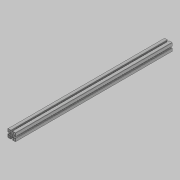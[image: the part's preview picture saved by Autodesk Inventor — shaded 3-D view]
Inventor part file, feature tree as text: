
AUTODESK INVENTOR PART (.ipt)
format: ipt  version: 2021.2 (Build 252289000, 289)  size: 202,240 bytes
history: native  units: in
note: dims shown in document units (in); Inventor stores cm internally (conversion verified against a paired STEP export)
features: other x2, extrude x1, sketch x1, projected_geometry x1
ambient origin geometry x8: Origin, YZ Plane, XZ Plane, XY Plane, X Axis, Y Axis, Z Axis, Center Point
bodies: Body1 (feature_tree)
feature tree (5):
  other  "ソリッド2"
  extrude  "押し出し1"  Depth=23.622in
  sketch  "スケッチ2"
  projected_geometry  "投影ループ1"
  other  "ソリッド1"
